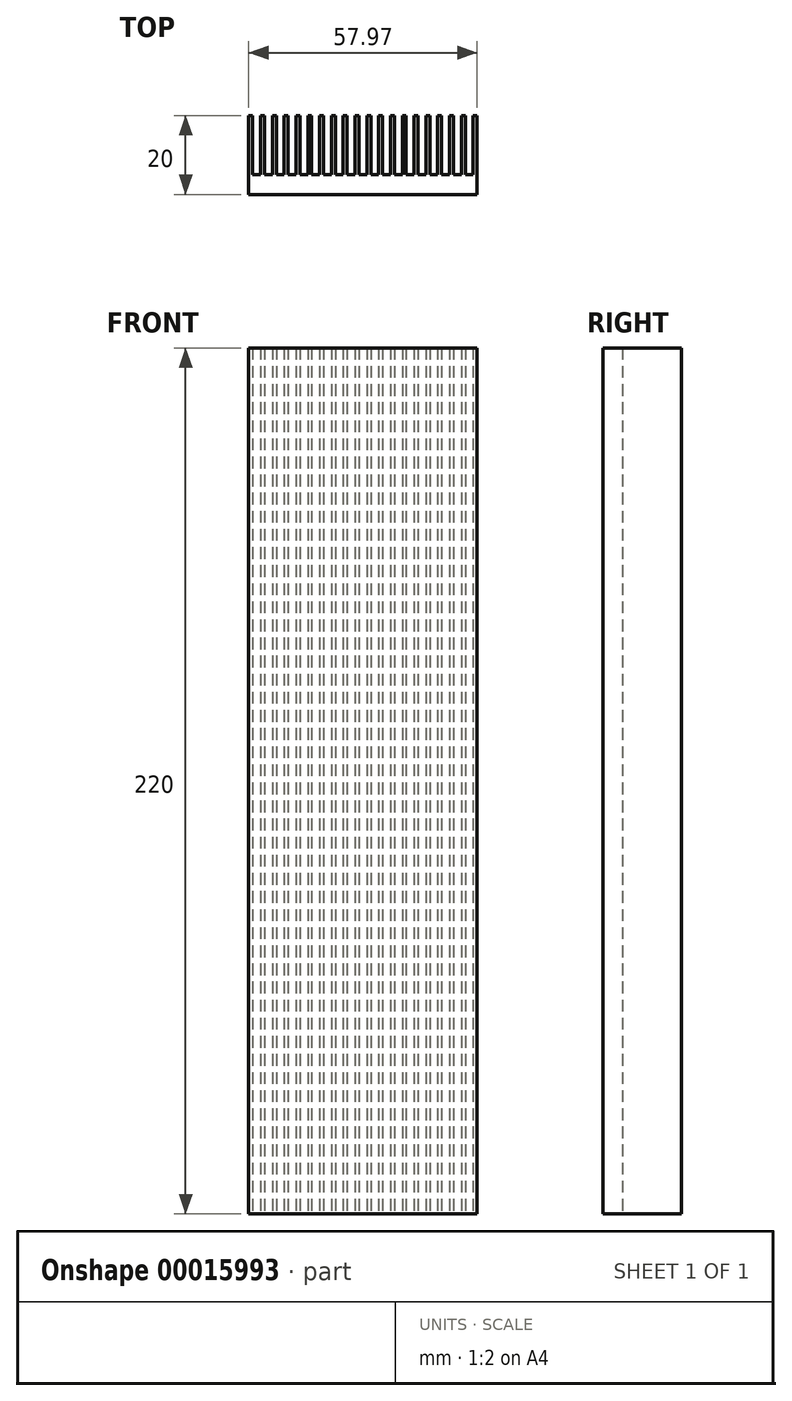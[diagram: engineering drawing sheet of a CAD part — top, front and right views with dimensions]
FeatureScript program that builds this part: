
annotation { "Feature Type Name" : "Feature", "Feature Type Description" : "" }
export const myFeature = defineFeature(function(context is Context, id is Id, definition is map)
    precondition{}
    {
        {
            var Q0;
            Q0=qCreatedBy(makeId("Top.planeOp"),FACE);
            var sketch = newSketch(context, id + "F0", { "sketchPlane" : qUnion([Q0])});
            skLineSegment(sketch, "E0", {"start": v(0, 0) * mm, "end": v(0, 20) * mm});
            skLineSegment(sketch, "E1", {"start": v(0, 20) * mm, "end": v(1, 20) * mm});
            skLineSegment(sketch, "E2", {"start": v(1, 20) * mm, "end": v(1, 5) * mm});
            skLineSegment(sketch, "E3", {"start": v(1, 5) * mm, "end": v(3, 5) * mm});
            skLineSegment(sketch, "E4", {"start": v(3, 5) * mm, "end": v(3, 20) * mm});
            skLineSegment(sketch, "E5.1.0.0", {"start": v(3, 20) * mm, "end": v(4, 20) * mm});
            skLineSegment(sketch, "E5.1.0.1", {"start": v(4, 20) * mm, "end": v(4, 5) * mm});
            skLineSegment(sketch, "E5.1.0.2", {"start": v(4, 5) * mm, "end": v(6, 5) * mm});
            skLineSegment(sketch, "E5.1.0.3", {"start": v(6, 5) * mm, "end": v(6, 20) * mm});
            skLineSegment(sketch, "E5.2.0.0", {"start": v(6, 20) * mm, "end": v(7, 20) * mm});
            skLineSegment(sketch, "E5.2.0.1", {"start": v(7, 20) * mm, "end": v(7, 5) * mm});
            skLineSegment(sketch, "E5.2.0.2", {"start": v(7, 5) * mm, "end": v(9, 5) * mm});
            skLineSegment(sketch, "E5.2.0.3", {"start": v(9, 5) * mm, "end": v(9, 20) * mm});
            skLineSegment(sketch, "E5.3.0.0", {"start": v(9, 20) * mm, "end": v(10, 20) * mm});
            skLineSegment(sketch, "E5.3.0.1", {"start": v(10, 20) * mm, "end": v(10, 5) * mm});
            skLineSegment(sketch, "E5.3.0.2", {"start": v(10, 5) * mm, "end": v(12, 5) * mm});
            skLineSegment(sketch, "E5.3.0.3", {"start": v(12, 5) * mm, "end": v(12, 20) * mm});
            skLineSegment(sketch, "E5.4.0.0", {"start": v(12, 20) * mm, "end": v(13, 20) * mm});
            skLineSegment(sketch, "E5.4.0.1", {"start": v(13, 20) * mm, "end": v(13, 5) * mm});
            skLineSegment(sketch, "E5.4.0.2", {"start": v(13, 5) * mm, "end": v(15, 5) * mm});
            skLineSegment(sketch, "E5.4.0.3", {"start": v(15, 5) * mm, "end": v(15, 20) * mm});
            skLineSegment(sketch, "E5.5.0.0", {"start": v(15, 20) * mm, "end": v(16, 20) * mm});
            skLineSegment(sketch, "E5.5.0.1", {"start": v(16, 20) * mm, "end": v(16, 5) * mm});
            skLineSegment(sketch, "E5.5.0.2", {"start": v(16, 5) * mm, "end": v(18, 5) * mm});
            skLineSegment(sketch, "E5.5.0.3", {"start": v(18, 5) * mm, "end": v(18, 20) * mm});
            skLineSegment(sketch, "E5.6.0.0", {"start": v(18, 20) * mm, "end": v(19, 20) * mm});
            skLineSegment(sketch, "E5.6.0.1", {"start": v(19, 20) * mm, "end": v(19, 5) * mm});
            skLineSegment(sketch, "E5.6.0.2", {"start": v(19, 5) * mm, "end": v(21, 5) * mm});
            skLineSegment(sketch, "E5.6.0.3", {"start": v(21, 5) * mm, "end": v(21, 20) * mm});
            skLineSegment(sketch, "E5.7.0.0", {"start": v(21, 20) * mm, "end": v(22, 20) * mm});
            skLineSegment(sketch, "E5.7.0.1", {"start": v(22, 20) * mm, "end": v(22, 5) * mm});
            skLineSegment(sketch, "E5.7.0.2", {"start": v(22, 5) * mm, "end": v(24, 5) * mm});
            skLineSegment(sketch, "E5.7.0.3", {"start": v(24, 5) * mm, "end": v(24, 20) * mm});
            skLineSegment(sketch, "E5.8.0.0", {"start": v(24, 20) * mm, "end": v(25, 20) * mm});
            skLineSegment(sketch, "E5.8.0.1", {"start": v(25, 20) * mm, "end": v(25, 5) * mm});
            skLineSegment(sketch, "E5.8.0.2", {"start": v(25, 5) * mm, "end": v(27, 5) * mm});
            skLineSegment(sketch, "E5.8.0.3", {"start": v(27, 5) * mm, "end": v(27, 20) * mm});
            skLineSegment(sketch, "E5.9.0.0", {"start": v(27, 20) * mm, "end": v(28, 20) * mm});
            skLineSegment(sketch, "E5.9.0.1", {"start": v(28, 20) * mm, "end": v(28, 5) * mm});
            skLineSegment(sketch, "E5.9.0.2", {"start": v(28, 5) * mm, "end": v(30, 5) * mm});
            skLineSegment(sketch, "E5.9.0.3", {"start": v(30, 5) * mm, "end": v(30, 20) * mm});
            skLineSegment(sketch, "E5.10.0.0", {"start": v(30, 20) * mm, "end": v(31, 20) * mm});
            skLineSegment(sketch, "E5.10.0.1", {"start": v(31, 20) * mm, "end": v(31, 5) * mm});
            skLineSegment(sketch, "E5.10.0.2", {"start": v(31, 5) * mm, "end": v(33, 5) * mm});
            skLineSegment(sketch, "E5.10.0.3", {"start": v(33, 5) * mm, "end": v(33, 20) * mm});
            skLineSegment(sketch, "E5.11.0.0", {"start": v(33, 20) * mm, "end": v(34, 20) * mm});
            skLineSegment(sketch, "E5.11.0.1", {"start": v(34, 20) * mm, "end": v(34, 5) * mm});
            skLineSegment(sketch, "E5.11.0.2", {"start": v(34, 5) * mm, "end": v(36, 5) * mm});
            skLineSegment(sketch, "E5.11.0.3", {"start": v(36, 5) * mm, "end": v(36, 20) * mm});
            skLineSegment(sketch, "E5.12.0.0", {"start": v(36, 20) * mm, "end": v(37, 20) * mm});
            skLineSegment(sketch, "E5.12.0.1", {"start": v(37, 20) * mm, "end": v(37, 5) * mm});
            skLineSegment(sketch, "E5.12.0.2", {"start": v(37, 5) * mm, "end": v(39, 5) * mm});
            skLineSegment(sketch, "E5.12.0.3", {"start": v(39, 5) * mm, "end": v(39, 20) * mm});
            skLineSegment(sketch, "E5.13.0.0", {"start": v(39, 20) * mm, "end": v(40, 20) * mm});
            skLineSegment(sketch, "E5.13.0.1", {"start": v(40, 20) * mm, "end": v(40, 5) * mm});
            skLineSegment(sketch, "E5.13.0.2", {"start": v(40, 5) * mm, "end": v(42, 5) * mm});
            skLineSegment(sketch, "E5.13.0.3", {"start": v(42, 5) * mm, "end": v(42, 20) * mm});
            skLineSegment(sketch, "E5.14.0.0", {"start": v(42, 20) * mm, "end": v(43, 20) * mm});
            skLineSegment(sketch, "E5.14.0.1", {"start": v(43, 20) * mm, "end": v(43, 5) * mm});
            skLineSegment(sketch, "E5.14.0.2", {"start": v(43, 5) * mm, "end": v(45, 5) * mm});
            skLineSegment(sketch, "E5.14.0.3", {"start": v(45, 5) * mm, "end": v(45, 20) * mm});
            skLineSegment(sketch, "E5.15.0.0", {"start": v(45, 20) * mm, "end": v(46, 20) * mm});
            skLineSegment(sketch, "E5.15.0.1", {"start": v(46, 20) * mm, "end": v(46, 5) * mm});
            skLineSegment(sketch, "E5.15.0.2", {"start": v(46, 5) * mm, "end": v(48, 5) * mm});
            skLineSegment(sketch, "E5.15.0.3", {"start": v(48, 5) * mm, "end": v(48, 20) * mm});
            skLineSegment(sketch, "E5.16.0.0", {"start": v(48, 20) * mm, "end": v(49, 20) * mm});
            skLineSegment(sketch, "E5.16.0.1", {"start": v(49, 20) * mm, "end": v(49, 5) * mm});
            skLineSegment(sketch, "E5.16.0.2", {"start": v(49, 5) * mm, "end": v(51, 5) * mm});
            skLineSegment(sketch, "E5.16.0.3", {"start": v(51, 5) * mm, "end": v(51, 20) * mm});
            skLineSegment(sketch, "E5.17.0.0", {"start": v(51, 20) * mm, "end": v(52, 20) * mm});
            skLineSegment(sketch, "E5.17.0.1", {"start": v(52, 20) * mm, "end": v(52, 5) * mm});
            skLineSegment(sketch, "E5.17.0.2", {"start": v(52, 5) * mm, "end": v(54, 5) * mm});
            skLineSegment(sketch, "E5.17.0.3", {"start": v(54, 5) * mm, "end": v(54, 20) * mm});
            skLineSegment(sketch, "E5.18.0.0", {"start": v(54, 20) * mm, "end": v(55, 20) * mm});
            skLineSegment(sketch, "E5.18.0.1", {"start": v(55, 20) * mm, "end": v(55, 5) * mm});
            skLineSegment(sketch, "E5.18.0.2", {"start": v(55, 5) * mm, "end": v(57, 5) * mm});
            skLineSegment(sketch, "E5.18.0.3", {"start": v(57, 5) * mm, "end": v(57, 20) * mm});
            skLineSegment(sketch, "E5.19.0.0", {"start": v(57, 20) * mm, "end": v(57.97, 20) * mm});
            skLineSegment(sketch, "E5.19.0.1", {"start": v(57.97, 20) * mm, "end": v(57.97, 0) * mm});
            skLineSegment(sketch, "E6", {"start": v(0, 0) * mm, "end": v(57.97, 0) * mm});
            skSolve(sketch);
        }
        {
            var Q0;
            Q0 = qSketchRegion(id + "F0", true);
            extrude(context, id + "F1", {"entities" : qUnion([Q0]), "depth" : 220 * mm});
        }
    });
